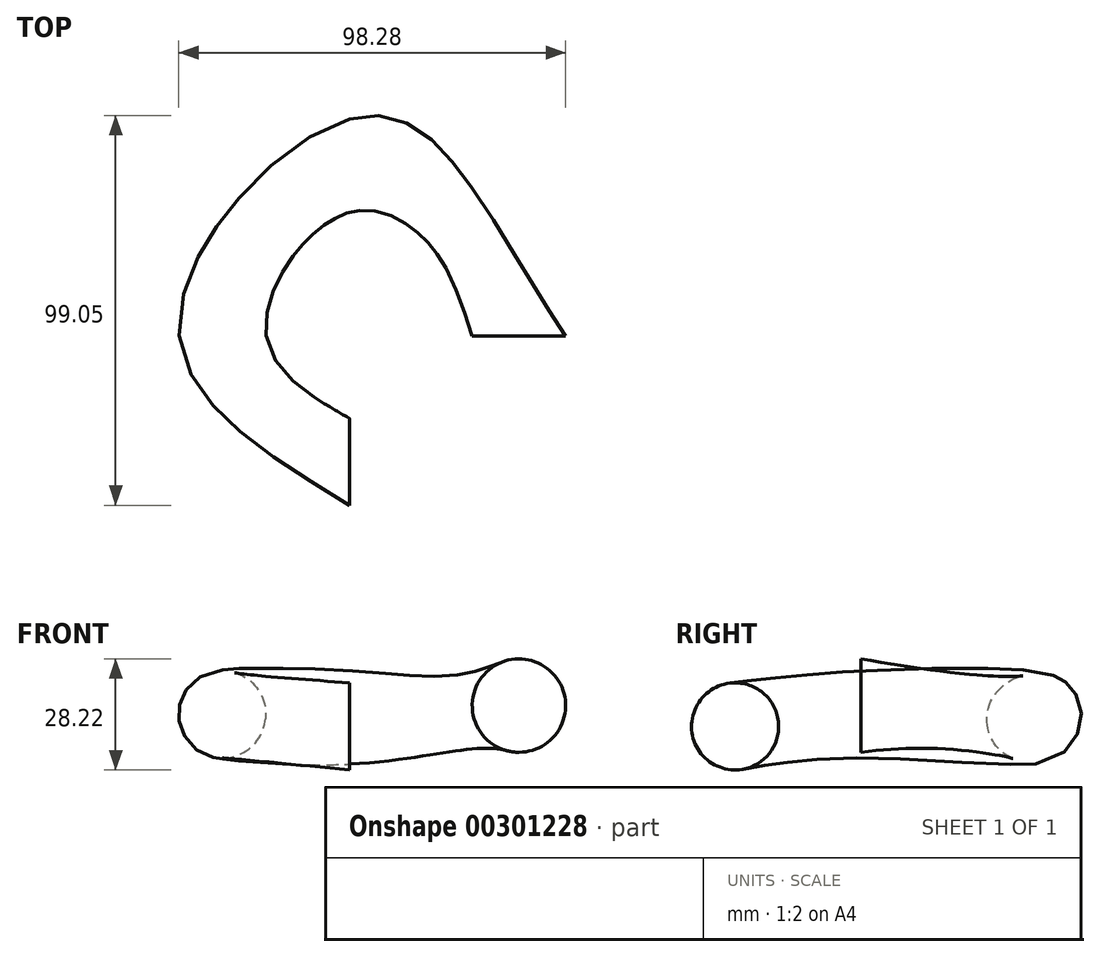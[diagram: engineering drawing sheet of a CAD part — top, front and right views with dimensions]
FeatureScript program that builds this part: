
annotation { "Feature Type Name" : "Feature", "Feature Type Description" : "" }
export const myFeature = defineFeature(function(context is Context, id is Id, definition is map)
    precondition{}
    {
        {
            var Q0;
            Q0=qCreatedBy(makeId("Front.planeOp"),FACE);
            var sketch = newSketch(context, id + "F0", { "sketchPlane" : qUnion([Q0])});
            skLineSegment(sketch, "E0", {"start": v(0, 46.5) * mm, "end": v(0, 0) * mm, "construction": true});
            skFitSpline(sketch, "E1", {"points": [v(0, 0) * mm, v(19.34, 51.14) * mm, v(43.04, 63.69) * mm], "startDerivative": vector(8.97, 132.26) * mm, "endDerivative": vector(78.2, 1.68) * mm, "construction": true});
            skFitSpline(sketch, "E2.MirrorCS", {"points": [v(0, 0) * mm, v(-19.34, 51.14) * mm, v(-43.04, 63.69) * mm], "startDerivative": vector(-8.97, 132.26) * mm, "endDerivative": vector(-78.2, 1.68) * mm, "construction": true});
            skCircle(sketch, "E3", {"center": v(43.04, 63.69) * mm, "radius": 11.86 * mm});
            skCircle(sketch, "E4", {"center": v(22.3, 54.33) * mm, "radius": 10.88 * mm});
            skCircle(sketch, "E5", {"center": v(10.68, 39.02) * mm, "radius": 8.34 * mm});
            skCircle(sketch, "E6", {"center": v(5.15, 26.78) * mm, "radius": 5.08 * mm});
            skCircle(sketch, "E7", {"center": v(2.93, 19.32) * mm, "radius": 2.7 * mm});
            skCircle(sketch, "E8", {"center": v(1.99, 15.14) * mm, "radius": 1.58 * mm});
            skCircle(sketch, "E9", {"center": v(1.55, 12.84) * mm, "radius": 0.76 * mm});
            skCircle(sketch, "E10", {"center": v(1.25, 11.09) * mm, "radius": 1.02 * mm});
            skCircle(sketch, "E11", {"center": v(0.99, 9.38) * mm, "radius": 0.71 * mm});
            skCircle(sketch, "E12", {"center": v(-32.22, 61.4) * mm, "radius": 11.06 * mm});
            skCircle(sketch, "E13", {"center": v(-15.6, 46.54) * mm, "radius": 11.23 * mm});
            skCircle(sketch, "E14", {"center": v(-6.71, 30.88) * mm, "radius": 6.78 * mm});
            skCircle(sketch, "E15", {"center": v(-3.52, 21.55) * mm, "radius": 3.08 * mm});
            skCircle(sketch, "E16", {"center": v(-2.28, 16.52) * mm, "radius": 2.1 * mm});
            skCircle(sketch, "E17", {"center": v(-1.6, 13.08) * mm, "radius": 1.4 * mm});
            skSolve(sketch);
        }
        {
            var Q0;
            Q0=qCreatedBy(makeId("Right.planeOp"),FACE);
            var sketch = newSketch(context, id + "F1", { "sketchPlane" : qUnion([Q0])});
            skLineSegment(sketch, "E18", {"start": v(0.2, 43.48) * mm, "end": v(0.2, -2.77) * mm, "construction": true});
            skFitSpline(sketch, "E19", {"points": [v(0.2, -2.77) * mm, v(19.1, 47.61) * mm, v(43.25, 60.68) * mm], "startDerivative": vector(9.25, 129.39) * mm, "endDerivative": vector(77.06, 0.82) * mm, "construction": true});
            skFitSpline(sketch, "E20.MirrorCS", {"points": [v(0.2, -2.77) * mm, v(-18.68, 47.61) * mm, v(-42.84, 60.67) * mm], "startDerivative": vector(-9.26, 129.39) * mm, "endDerivative": vector(-77.06, 0.82) * mm, "construction": true});
            skCircle(sketch, "E21", {"center": v(43.25, 60.68) * mm, "radius": 11.86 * mm});
            skCircle(sketch, "E22", {"center": v(22.52, 51.32) * mm, "radius": 10.88 * mm});
            skCircle(sketch, "E23", {"center": v(10.89, 36) * mm, "radius": 8.34 * mm});
            skCircle(sketch, "E24", {"center": v(5.36, 23.77) * mm, "radius": 5.08 * mm});
            skCircle(sketch, "E25", {"center": v(3.14, 16.3) * mm, "radius": 2.7 * mm});
            skCircle(sketch, "E26", {"center": v(2.2, 12.13) * mm, "radius": 1.58 * mm});
            skCircle(sketch, "E27", {"center": v(1.75, 9.83) * mm, "radius": 0.76 * mm});
            skCircle(sketch, "E28", {"center": v(1.46, 8.08) * mm, "radius": 1.02 * mm});
            skCircle(sketch, "E29", {"center": v(1.2, 6.37) * mm, "radius": 0.71 * mm});
            skCircle(sketch, "E30", {"center": v(-32, 58.4) * mm, "radius": 11.06 * mm});
            skCircle(sketch, "E31", {"center": v(-15.4, 43.53) * mm, "radius": 11.23 * mm});
            skCircle(sketch, "E32", {"center": v(-6.5, 27.87) * mm, "radius": 6.78 * mm});
            skCircle(sketch, "E33", {"center": v(-3.31, 18.54) * mm, "radius": 3.08 * mm});
            skCircle(sketch, "E34", {"center": v(-2.07, 13.5) * mm, "radius": 2.1 * mm});
            skCircle(sketch, "E35", {"center": v(-1.38, 10.07) * mm, "radius": 1.4 * mm});
            skSolve(sketch);
        }
        {
            var Q0;
            Q0=makeQuery(id+"F0.imprint","IMPRINT",FACE,{"disambiguationData":[TD([[makeQuery(id+"F0.imprint","IMPRINT",EDGE,{"derivedFrom":sQuery(id+"F0.wireOp",EDGE,"E3")}),1.0]])]});
            var Q1;
            Q1=makeQuery(id+"F1.imprint","IMPRINT",FACE,{"disambiguationData":[TD([[makeQuery(id+"F1.imprint","IMPRINT",EDGE,{"derivedFrom":sQuery(id+"F1.wireOp",EDGE,"E21")}),1.0]])]});
            var Q2;
            Q2=makeQuery(id+"F0.imprint","IMPRINT",FACE,{"disambiguationData":[TD([[makeQuery(id+"F0.imprint","IMPRINT",EDGE,{"derivedFrom":sQuery(id+"F0.wireOp",EDGE,"E12")}),1.0]])]});
            var Q3;
            Q3=makeQuery(id+"F1.imprint","IMPRINT",FACE,{"disambiguationData":[TD([[makeQuery(id+"F1.imprint","IMPRINT",EDGE,{"derivedFrom":sQuery(id+"F1.wireOp",EDGE,"E30")}),1.0]])]});
            loft(context, id + "F2", {"sheetProfilesArray" : [{ "sheetProfileEntities" : qUnion([Q0]) }, { "sheetProfileEntities" : qUnion([Q1]) }, { "sheetProfileEntities" : qUnion([Q2]) }, { "sheetProfileEntities" : qUnion([Q3]) }]});
        }
    });
